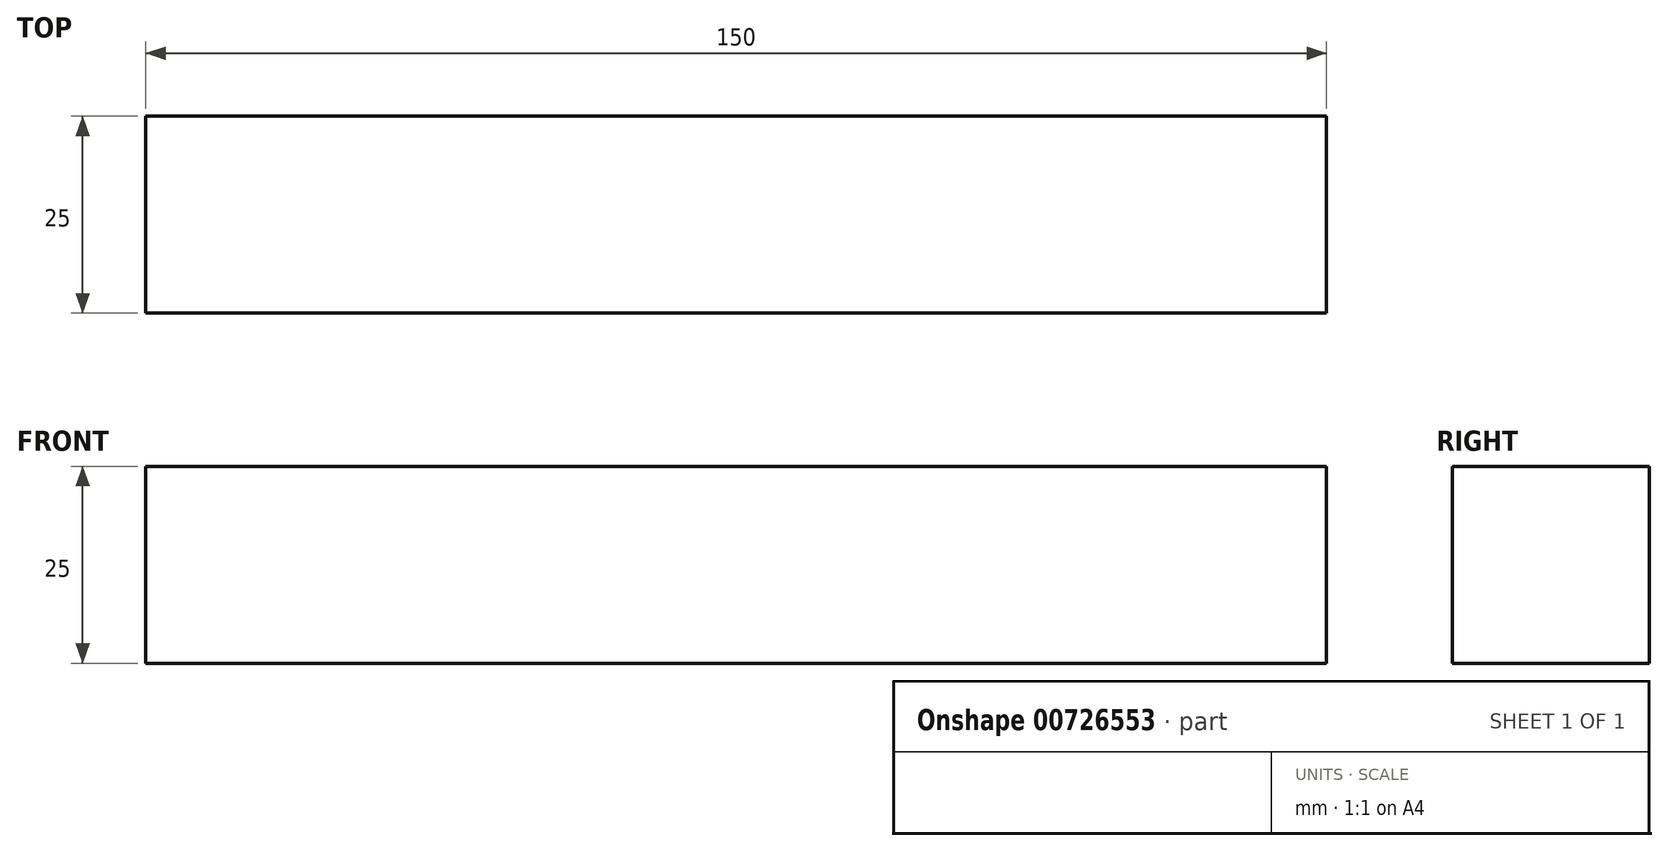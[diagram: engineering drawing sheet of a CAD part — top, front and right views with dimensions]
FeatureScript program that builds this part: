
annotation { "Feature Type Name" : "Feature", "Feature Type Description" : "" }
export const myFeature = defineFeature(function(context is Context, id is Id, definition is map)
    precondition{}
    {
        {
            var Q0;
            Q0=qCreatedBy(makeId("Top.planeOp"),FACE);
            var sketch = newSketch(context, id + "F0", { "sketchPlane" : qUnion([Q0])});
            skLineSegment(sketch, "E0.bottom", {"start": v(-73.17, 23.24) * mm, "end": v(76.83, 23.24) * mm});
            skLineSegment(sketch, "E0.top", {"start": v(-73.17, -1.76) * mm, "end": v(76.83, -1.76) * mm});
            skLineSegment(sketch, "E0.left", {"start": v(-73.17, 23.24) * mm, "end": v(-73.17, -1.76) * mm});
            skLineSegment(sketch, "E0.right", {"start": v(76.83, 23.24) * mm, "end": v(76.83, -1.76) * mm});
            skSolve(sketch);
        }
        {
            var Q0;
            Q0=makeQuery(id+"F0.imprint","IMPRINT",FACE,{"disambiguationData":[TD([[makeQuery(id+"F0.imprint","IMPRINT",EDGE,{"derivedFrom":sQuery(id+"F0.wireOp",EDGE,"E0.bottom")}),-1.0]])]});
            extrude(context, id + "F1", {"entities" : qUnion([Q0]), "depth" : 25 * mm, "offsetDistance" : 25 * mm});
        }
    });
